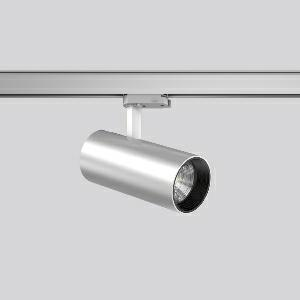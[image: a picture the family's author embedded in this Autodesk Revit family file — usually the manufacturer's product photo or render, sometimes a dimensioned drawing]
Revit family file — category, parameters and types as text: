
# Revit family: deecos_s_mini_742206_004_1_76_2d03
name_source: partatom
category: Lighting Fixtures
units: mm (PartAtom-declared; Revit-internal decimal feet)

## family parameters
Cut with Voids When Loaded = No
Host = Face
Light Source = No
Part Type = Normal
Room Calculation Point = No
Round Connector Dimension = Use Diameter
Shared = No

## types (1)
- DEECOS S mini (1 x LED Modul 940, 3400 lm, 4000)
    Apparent Load = 29 VA
    Approval mark = CE
    CIE Flux Codes = 99 100 100 100 100
    Color Rendering = 92
    Color Temperature = 4000
    Default Elevation = 1800 mm
    Description = Series: DEECOS S mini
LED surface-mounted projector in modern design with no visible cooling ribs. Housing: die-cast aluminium, powder-coated. Rotation range: 356°. Swivel range: 90°. Black plastic ring and recessed LED to prevent glare from the side. Optical assembly with lens made of plastic (polycarbonate) for the best homogeneous light distribution - can be changed without tools. Best colour rendering index Ra>90. With adapter for RZB 3-circuit DALI tracks. Suitable for Track on ceiling, Wall track. High quality converter without flickering and stroboscopic effect. The following accessories can be mounted without use of tools: interchangeable lenses, decorative glasses, honeycomb louvre, clear and frosted diffusers, white interchangeable plastic ring. 
Colour: silver
Diameter: 87 mm
Height: 214 mm
Lamp: LED
Socket: without socket
Colour temperature: 4000K
Colour rendering index (CRI): 92
System power: 29 W
Rated luminous flux: 3400 lm
Luminous efficiency: 117 lm/W
Control gear: Converter, dimmable, DALI
Protection class: I
Type of protection: IP 20
    Height = 214 mm
    Lamp = 1 x LED Modul 940
    Lamp Light Flux = 3400 lm
    Lamp count = 1
    Length = 87 mm
    Lifetime = 50000 h
    Luminous efficacy = 117 lm/W
    Manufacturer = RZB
    ModVariant = No
    Model = 742206.004.1.76
    Mounting Place = Ceiling
    Mounting Type = Rail mounted
    Number of Poles = 1
    OnlyDefault = Yes
    Power Factor = 1
    Product Name = DEECOS S mini
    Product group = Track mounted projectors
    ProductGroupID = 301
    Protection Class = Protection class I
    Protection Degree = IP 20
    RLX_Detail_Level = 1
    RLX_Emergency_Light_Flux = 0 lm
    RLX_Emergency_Type = 0
    RLX_Emergency_Type_DB = No
    RlxData = <blob elided: 37129 chars, md5=1cb2aacd>
    Socket = socket
    Standby Power = 0 W
    System Light Flux = 3400 lm
    System Power = 29 W
    Type Comments = Product without accessories
    Type Image = 741930.004.jpg
    URL = http://relux.com
    VarID = ---
    Voltage = 230 V
    Voltage Range = 220-240 V
    Weight = 0.00 kg
    Width = 0 mm  [stored 0 ft]

note: [stored X ft] marks values corroborated as IEEE doubles in the binary element streams (Revit-internal decimal feet)

## geometry (parser evidence)
native form markers: Blend x4, Sweep x13
no freeform markers — native parametric forms only
